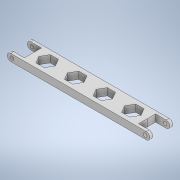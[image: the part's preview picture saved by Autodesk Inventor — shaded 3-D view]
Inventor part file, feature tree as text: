
AUTODESK INVENTOR PART (.ipt)
format: ipt  version: 2021.2 (Build 252289000, 289)  size: 175,104 bytes
history: native  units: in
note: dims shown in document units (in); Inventor stores cm internally (conversion verified against a paired STEP export)
features: sketch x3, extrude x2, hole x1, fillet x1
ambient origin geometry x8: Origin, YZ Plane, XZ Plane, XY Plane, X Axis, Y Axis, Z Axis, Center Point
bodies: Solid1 (feature_tree)
feature tree (7):
  extrude  "Extrusion1"  Depth=2.335in
  hole  "Hole1"  [1 undecoded]
  fillet  "Fillet2"  Radius=0.5in
  extrude  "Extrusion2"  TaperAngle=0.0deg  [1 undecoded]
  sketch  "Sketch1"  dims[d7=0.0in d8=2.335in]
  sketch  "Sketch2"  dims[d9=0.129in d10=0.224in d11=0.225in d12=0.25in d13=0.5635in d14=0.349in d15=0.8108in d18=0.5in d19=0.5in]
  sketch  "Sketch5"  dims[d20=1.5748in d22=1.0in d23=0.3937in d25=1.0in d27=0.0in d28=0.0in]
note: 2 required parameter values undecoded (feature->parameter linkage not recoverable at this tier; creation-order binding heuristic only, values carry confidence <= 0.55)
